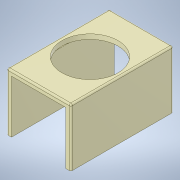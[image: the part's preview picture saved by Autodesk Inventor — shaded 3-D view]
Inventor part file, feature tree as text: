
AUTODESK INVENTOR PART (.ipt)
format: ipt  version: 2022 (Build 260153000, 153)  size: 134,656 bytes
history: native  units: in
note: dims shown in document units (in); Inventor stores cm internally (conversion verified against a paired STEP export)
features: other x2, sketch x2, extrude x1, fillet x1, hole x1
ambient origin geometry x8: Origin, YZ Plane, XZ Plane, XY Plane, X Axis, Y Axis, Z Axis, Center Point
bodies: Solid1 (feature_tree)
feature tree (7):
  other  "Annotations"
  extrude  "Extrusion1"  Depth=2.5in
  fillet  "Fillet1"  Radius=0.1875in
  hole  "Hole1"  [1 undecoded]
  sketch  "Sketch1"  dims[d0=2.25in d1=2.5in d2=0.1875in]
  sketch  "Sketch2"  dims[d3=0.1875in d4=0.1875in d5=4.0in d6=0.0in d7=0.0625in d8=2.0in d9=1.25in d10=2.1875in d11=0.6099in d12=0.0246in d13=2.1886in d14=0.375in d15=0.25in d16=0.5635in d17=0.1875in d18=0.0in]
  other  "General Note 1"
note: 1 required parameter value undecoded (feature->parameter linkage not recoverable at this tier; creation-order binding heuristic only, values carry confidence <= 0.55)
